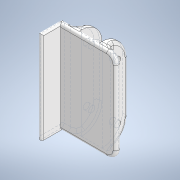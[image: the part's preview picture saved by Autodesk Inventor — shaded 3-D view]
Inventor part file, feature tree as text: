
AUTODESK INVENTOR PART (.ipt)
format: ipt  version: 2020.3 (Build 243373000, 373)  size: 299,520 bytes
history: native  units: mm
features: fillet x5, sketch x4, extrude x3, other x1, hole x1
ambient origin geometry x8: Origin, YZ Plane, XZ Plane, XY Plane, X Axis, Y Axis, Z Axis, Center Point
bodies: Body1 (feature_tree)
feature tree (14):
  other  "ソリッド1"
  extrude  "押し出し1"  Depth=32.0mm
  extrude  "押し出し2"  Depth=50.0mm
  extrude  "押し出し3"  Depth=3.0mm TaperAngle=0.0deg
  fillet  "フィレット1"  Radius=30.0mm
  fillet  "フィレット2"  Radius=10.0mm
  fillet  "フィレット3"  Radius=11.0mm
  fillet  "フィレット4"  Radius=3.0mm
  fillet  "フィレット5"  Radius=3.0mm
  hole  "穴1"  [1 undecoded]
  sketch  "スケッチ1"
  sketch  "スケッチ2"
  sketch  "スケッチ3"
  sketch  "スケッチ4"
note: 1 required parameter value undecoded (feature->parameter linkage not recoverable at this tier; creation-order binding heuristic only, values carry confidence <= 0.55)
